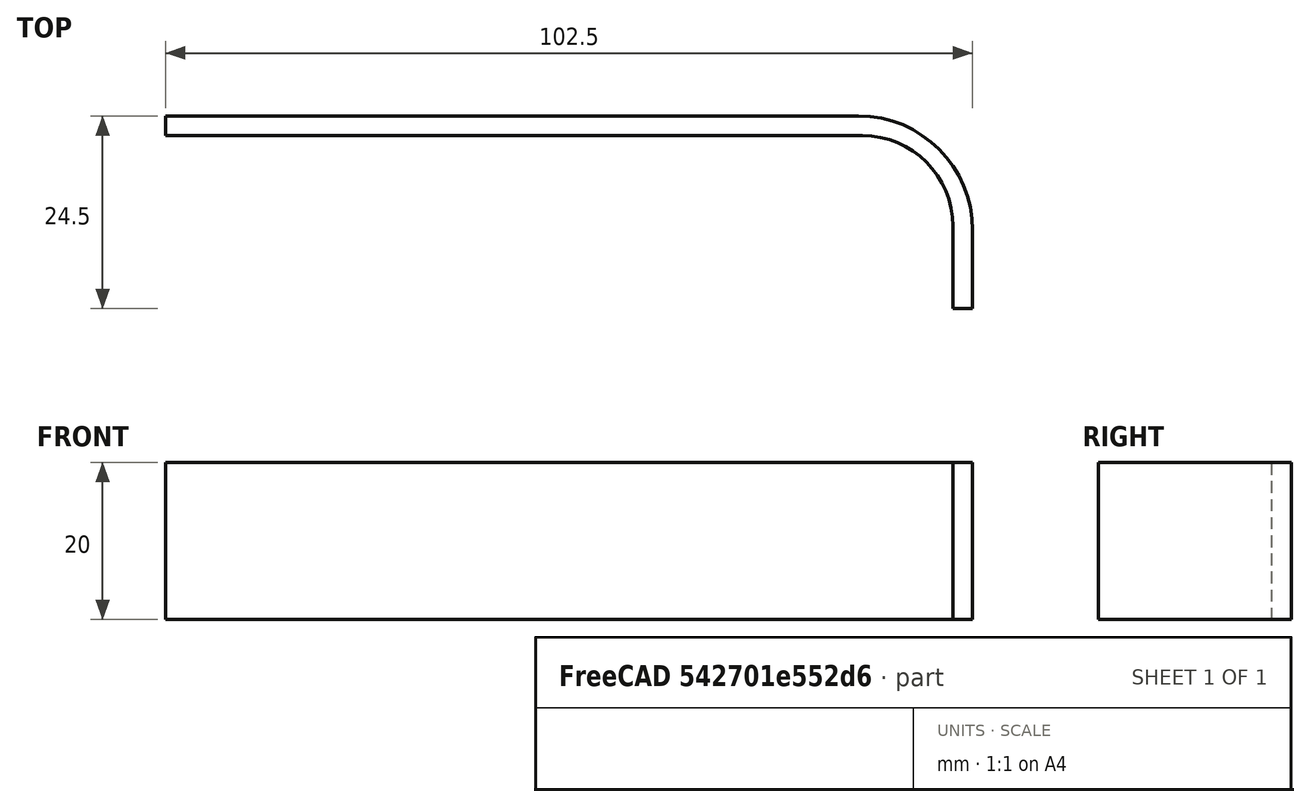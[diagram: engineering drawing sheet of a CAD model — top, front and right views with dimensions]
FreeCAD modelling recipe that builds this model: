
FCSTD DOCUMENT  (FreeCAD 1.0R39109 (Git))
Label: Gerüst-Kameraständer-DerGerät
License: All rights reserved
LicenseURL: https://en.wikipedia.org/wiki/All_rights_reserved
objects: Sketcher::SketchObject×1, PartDesign::Pad×1, PartDesign::Body×1
note: 6 computed .brp shape members not serialized (recipe doc carries the construction recipe); baked Part::Feature solids carry a one-line shape summary decoded from their .brp

FEATURE [Sketcher::SketchObject] Sketch
  ArcFitTolerance = 1e-06
  AttachmentSupport = -> [XZ_Plane]
  FullyConstrained = false
  MakeInternals = false
  MapMode = 5
  Placement = pos=(0,0,0) rot=(1,0,0;1.5708rad)
  sketch-geometry (12):
    g0: LineSegment StartX=0 StartY=2.5 StartZ=0 EndX=88 EndY=2.5 EndZ=0
    g1: ArcOfCircle CenterX=88 CenterY=-12 CenterZ=0 NormalX=0 NormalY=0 NormalZ=1 AngleXU=0 Radius=14.5 StartAngle=1e-16 EndAngle=1.5708
    g2: LineSegment StartX=102.5 StartY=-12 StartZ=0 EndX=102.5 EndY=-22 EndZ=0
    g3: LineSegment StartX=102.5 StartY=-22 StartZ=0 EndX=100 EndY=-22 EndZ=0
    g4: LineSegment StartX=100 StartY=-22 StartZ=0 EndX=100 EndY=-11.5 EndZ=0
    g5: ArcOfCircle CenterX=88.5 CenterY=-11.5 CenterZ=0 NormalX=0 NormalY=0 NormalZ=1 AngleXU=0 Radius=11.5 StartAngle=0 EndAngle=1.5708
    g6: LineSegment StartX=88.5 StartY=0 StartZ=0 EndX=0 EndY=0 EndZ=0
    g7: LineSegment StartX=0 StartY=0 StartZ=0 EndX=0 EndY=2.5 EndZ=0
    g8: LineSegment [constr] StartX=88 StartY=2.5 StartZ=0 EndX=88 EndY=64.8017 EndZ=0
    g9: LineSegment [constr] StartX=102.5 StartY=-12 StartZ=0 EndX=144.318 EndY=-12 EndZ=0
    g10: LineSegment [constr] StartX=88.5 StartY=0 StartZ=0 EndX=88.5 EndY=68.109 EndZ=0
    g11: LineSegment [constr] StartX=100 StartY=-11.5 StartZ=0 EndX=145.29 EndY=-11.5 EndZ=0
  constraints (29):
    c: Horizontal(g0)
    c: Tangent(g0,g1) = 1.5708
    c: Tangent(g1,g2) = 1.5708
    c: Coincident(g2,g3)
    c: Horizontal(g3)
    c: Coincident(g3,g4)
    c: Vertical(g4)
    c: Tangent(g4,g5) = -1.5708
    c: Horizontal(g6)
    c: Coincident(g6,g7)
    c: Coincident(g7,g0)
    c: Tangent(g5,g6) = -1.5708
    c: DistanceY(g7,g7) = 2.5
    c: Vertical(g2)
    c: Coincident(g8,g0)
    c: Vertical(g8)
    c: Coincident(g9,g1)
    c: Horizontal(g9)
    c: DistanceY(g1,g0) = 14.5
    c: Coincident(g10,g5)
    c: Vertical(g10)
    c: Coincident(g11,g4)
    c: Horizontal(g11)
    c: DistanceY(g5,g5) = 11.5
    c: DistanceY(g2,g2) = 10
    c: Vertical(g7)
    c: Coincident(g6,g-1)
    c: Distance(g-2,g4) = 100
    c: Distance(g4,g2) = 2.5
FEATURE [PartDesign::Pad] Pad
  Direction = (0,-1,2e-16)
  Length = 20
  Length2 = 10
  Placement = pos=(0,0,0) rot=(1,0,0;1.5708rad)
  Profile = -> Sketch
  ReferenceAxis = -> Sketch [N_Axis]
  Refine = true
  Suppressed = false
  Type = 0
FEATURE [PartDesign::Body] Body  label="Körper"
  AllowCompound = false
  Group = -> [Sketch,Pad]
  Origin = -> Origin
  Placement = pos=(0,0,0) rot=(-1,0,0;1.5708rad)
  Tip = -> Pad
